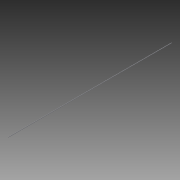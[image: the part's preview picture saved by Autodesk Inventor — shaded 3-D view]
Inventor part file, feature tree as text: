
AUTODESK INVENTOR PART (.ipt)
format: ipt  version: 2015 SP1 (Build 190203100, 203)  size: 64,000 bytes
history: native  units: in
note: dims shown in document units (in); Inventor stores cm internally (conversion verified against a paired STEP export)
features: extrude x1, sketch x1
ambient origin geometry x8: Origin, YZ Plane, XZ Plane, XY Plane, X Axis, Y Axis, Z Axis, Center Point
bodies: Solid1 (feature_tree)
feature tree (2):
  extrude  "Extrusion1"  Depth=39.0in TaperAngle=0.0deg
  sketch  "Sketch1"  dims[d0=0.125in d1=39.0in d2=0.0in]
